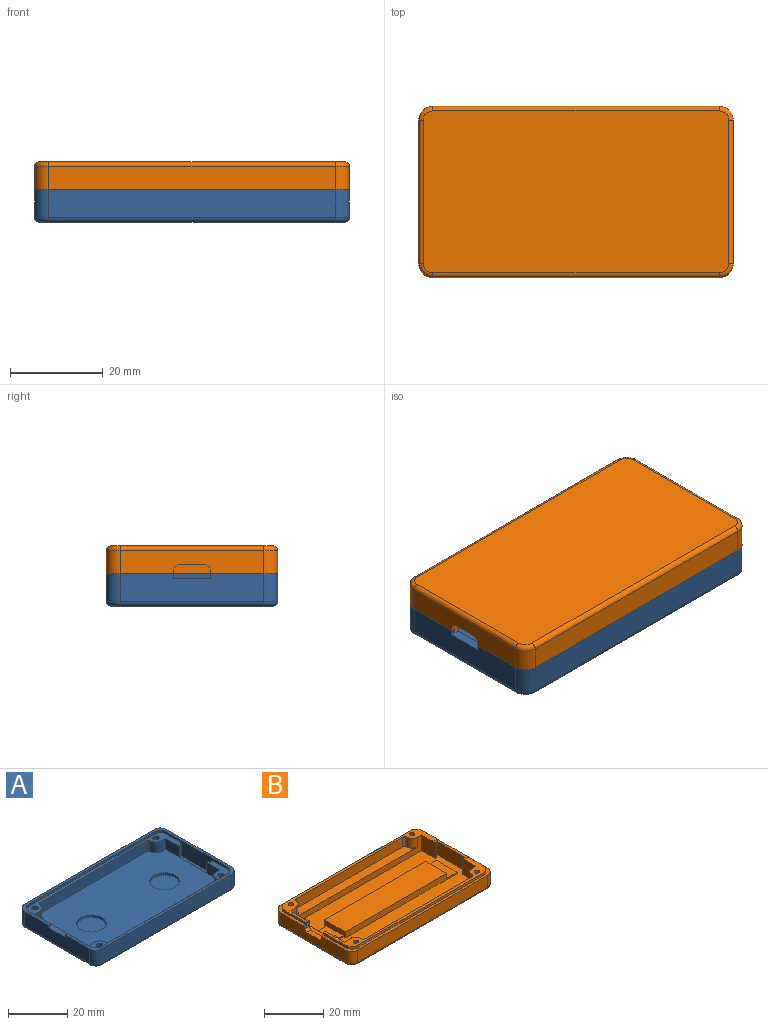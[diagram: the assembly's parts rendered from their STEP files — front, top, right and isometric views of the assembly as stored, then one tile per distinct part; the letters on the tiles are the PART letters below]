
ASSEMBLY  parts=2 mates=1
PART A: 74 faces, bbox 68.5x37.5x7 mm
  f0: plane 66x35mm, normal (0,0,-1), area 2263.6mm2, adj f43,f45,f47,f49,f52,f53,f54,f55
  f1: plane 29x6.5mm, normal (-1,0,0), area 111.5mm2, adj f12,f29,f30,f36,f51,f57,f58
  f2: plane 1x1mm, normal (0,1,0), area 1mm2, adj f6,f11,f12,f36
  f3: plane 62x6mm, normal (0,-1,0), area 372mm2, adj f12,f54,f68,f70
  f4: plane 31x6mm, normal (1,0,0), area 186mm2, adj f12,f52,f66,f68
  f5: plane 62x6mm, normal (0,1,0), area 372mm2, adj f12,f53,f64,f66
  f6: plane 31x6mm, normal (-1,0,0), area 178mm2, adj f2,f7,f12,f36,f55,f64,f70
  f7: plane 1x1mm, normal (0,-1,0), area 1mm2, adj f6,f8,f12,f36
  f8: plane 10.5x1mm, normal (1,0,0), area 10.5mm2, adj f7,f12,f36,f56
  f9: plane 60x1mm, normal (0,-1,0), area 60mm2, adj f12,f36,f56,f57
  f10: plane 60x1mm, normal (0,1,0), area 60mm2, adj f12,f36,f58,f59
  f11: plane 10.5x1mm, normal (1,0,0), area 10.5mm2, adj f2,f12,f36,f59
  f12: plane 68x37mm, normal (0,0,1), area 198mm2, adj f1,f2,f3,f4,f5,f6,f7,f8
  f13: plane 5.5x0.6mm, normal (0,1,0), area 3.3mm2, adj f14,f36,f37,f51,f72
  f14: plane 6.5x4.5mm, normal (-1,0,0), area 29.2mm2, adj f13,f15,f36,f40
  f15: plane 4.5x2mm, normal (0,1,0), area 9mm2, adj f14,f16,f36,f40
  f16: cylinder r=2.5mm len=4.5mm, axis (0,0,-1), area 17.7mm2, adj f15,f36,f40,f60
  f17: plane 51x4.5mm, normal (0,1,0), area 229.5mm2, adj f36,f40,f60,f61
  f18: cylinder r=2.5mm len=4.5mm, axis (0,0,-1), area 17.7mm2, adj f19,f36,f40,f61
  f19: plane 4.5x3mm, normal (0,1,0), area 13.5mm2, adj f18,f20,f36,f40
  f20: plane 26x4.5mm, normal (1,0,0), area 117mm2, adj f19,f21,f36,f40
  f21: plane 4.5x3mm, normal (0,-1,0), area 13.5mm2, adj f20,f22,f36,f40
  f22: cylinder r=2.5mm len=4.5mm, axis (0,0,-1), area 17.7mm2, adj f21,f36,f40,f62
  f23: plane 51x4.5mm, normal (0,-1,0), area 229.5mm2, adj f36,f40,f62,f63
  f24: cylinder r=2.5mm len=4.5mm, axis (0,0,-1), area 17.7mm2, adj f25,f36,f40,f63
  f25: plane 4.5x2mm, normal (0,-1,0), area 9mm2, adj f24,f26,f36,f40
  f26: plane 6.5x4.5mm, normal (-1,0,0), area 29.2mm2, adj f25,f27,f36,f40
  f27: plane 5.5x0.6mm, normal (0,-1,0), area 3.3mm2, adj f26,f36,f37,f51,f73
  f28: plane 5.5x0.7mm, normal (1,0,0), area 3.8mm2, adj f29,f36,f51,f73
  f29: plane 5.5x1.1mm, normal (0,-1,0), area 6mm2, adj f1,f28,f36,f51
  f30: plane 5.5x1.1mm, normal (0,1,0), area 6mm2, adj f1,f34,f36,f51
  f31: cylinder r=1.1mm len=3.5mm, axis (0,0,-1), area 24.2mm2, adj f36,f50
  f32: cylinder r=1.1mm len=3.5mm, axis (0,0,-1), area 24.2mm2, adj f36,f48
  f33: cylinder r=1.1mm len=3.5mm, axis (0,0,-1), area 24.2mm2, adj f36,f46
  f34: plane 5.5x0.7mm, normal (1,0,0), area 3.8mm2, adj f30,f36,f51,f72
  f35: cylinder r=1.1mm len=3.5mm, axis (0,0,-1), area 24.2mm2, adj f36,f44
  f36: plane 67x35mm, normal (0,0,1), area 253.3mm2, adj f1,f2,f6,f7,f8,f9,f10,f11
  f37: plane 13x1mm, normal (1,0,0), area 13mm2, adj f13,f27,f40,f51
  f38: cylinder r=5mm len=10mm, axis (0,0,-1), area 31.4mm2, adj f40,f41
  f39: cylinder r=5mm len=10mm, axis (0,0,-1), area 31.4mm2, adj f40,f42
  f40: plane 63x33mm, normal (0,0,1), area 1856.4mm2, adj f14,f15,f16,f17,f18,f19,f20,f21
  f41: plane 10x10mm, normal (0,0,1), area 78.5mm2, adj f38
  f42: plane 10x10mm, normal (0,0,1), area 78.5mm2, adj f39
  f43: cylinder r=1.85mm len=3.7mm, axis (0,0,-1), area 29.1mm2, adj f0,f44
  f44: plane 3.7x3.7mm, normal (0,0,-1), area 7mm2, adj f35,f43
  f45: cylinder r=1.85mm len=3.7mm, axis (0,0,-1), area 29.1mm2, adj f0,f46
  f46: plane 3.7x3.7mm, normal (0,0,-1), area 7mm2, adj f33,f45
  f47: cylinder r=1.85mm len=3.7mm, axis (0,0,-1), area 29.1mm2, adj f0,f48
  f48: plane 3.7x3.7mm, normal (0,0,-1), area 7mm2, adj f32,f47
  f49: cylinder r=1.85mm len=3.7mm, axis (0,0,-1), area 29.1mm2, adj f0,f50
  f50: plane 3.7x3.7mm, normal (0,0,-1), area 7mm2, adj f31,f49
  f51: plane 15x2mm, normal (0,0,1), area 28.3mm2, adj f1,f13,f27,f28,f29,f30,f34,f37
  f52: cylinder r=1mm len=31mm, axis (0,1,0), area 48.7mm2, adj f0,f4,f67,f69
  f53: cylinder r=1mm len=62mm, axis (-1,0,0), area 97.4mm2, adj f0,f5,f65,f67
  f54: cylinder r=1mm len=62mm, axis (1,0,0), area 97.4mm2, adj f0,f3,f69,f71
  f55: cylinder r=1mm len=31mm, axis (0,-1,0), area 48.7mm2, adj f0,f6,f65,f71
  f56: cylinder r=3mm len=3mm, axis (0,0,-1), area 4.7mm2, adj f8,f9,f12,f36
  f57: cylinder r=3mm len=3mm, axis (0,0,1), area 4.7mm2, adj f1,f9,f12,f36
  f58: cylinder r=3mm len=3mm, axis (0,0,-1), area 4.7mm2, adj f1,f10,f12,f36
  f59: cylinder r=3mm len=3mm, axis (0,0,1), area 4.7mm2, adj f10,f11,f12,f36
  f60: cylinder r=1mm len=4.5mm, axis (0,0,-1), area 7.1mm2, adj f16,f17,f36,f40
  f61: cylinder r=1mm len=4.5mm, axis (0,0,1), area 7.1mm2, adj f17,f18,f36,f40
  f62: cylinder r=1mm len=4.5mm, axis (0,0,1), area 7.1mm2, adj f22,f23,f36,f40
  f63: cylinder r=1mm len=4.5mm, axis (0,0,-1), area 7.1mm2, adj f23,f24,f36,f40
  f64: cylinder r=3mm len=6mm, axis (0,0,1), area 28.3mm2, adj f5,f6,f12,f65
  f65: torus R=2mm, axis (0,0,1), area 6.5mm2, adj f0,f53,f55,f64
  f66: cylinder r=3mm len=6mm, axis (0,0,-1), area 28.3mm2, adj f4,f5,f12,f67
  f67: torus R=2mm, axis (0,0,1), area 6.5mm2, adj f0,f52,f53,f66
  f68: cylinder r=3mm len=6mm, axis (0,0,1), area 28.3mm2, adj f3,f4,f12,f69
  f69: torus R=2mm, axis (0,0,1), area 6.5mm2, adj f0,f52,f54,f68
  f70: cylinder r=3mm len=6mm, axis (0,0,-1), area 28.3mm2, adj f3,f6,f12,f71
  f71: torus R=2mm, axis (0,0,1), area 6.5mm2, adj f0,f54,f55,f70
  f72: plane 5.5x0.3mm, normal (0.71,0.71,0), area 2.3mm2, adj f13,f34,f36,f51
  f73: plane 5.5x0.3mm, normal (0.71,-0.71,0), area 2.3mm2, adj f27,f28,f36,f51
PART B: 86 faces, bbox 68.5x37.5x7 mm
  f0: plane 62.5x26mm, normal (0,0,1), area 1018.3mm2, adj f2,f10,f18,f19,f20,f22,f25,f29
  f1: plane 66x35mm, normal (0,0,-1), area 2306.6mm2, adj f52,f53,f54,f55,f69,f71,f73,f75
  f2: plane 15x5.5mm, normal (-1,0,0), area 82.5mm2, adj f0,f9,f18,f25
  f3: plane 2x2mm, normal (0,1,0), area 3mm2, adj f7,f9,f14,f15,f24,f64
  f4: plane 62x5mm, normal (0,-1,0), area 310mm2, adj f9,f54,f72,f74
  f5: plane 31x5mm, normal (1,0,0), area 155mm2, adj f9,f52,f70,f72
  f6: plane 62x5mm, normal (0,1,0), area 310mm2, adj f9,f53,f68,f70
  f7: plane 31x5mm, normal (-1,0,0), area 140mm2, adj f3,f8,f9,f41,f55,f64,f65,f68
  f8: plane 2x2mm, normal (0,-1,0), area 3mm2, adj f7,f9,f14,f28,f38,f65
  f9: plane 68x37mm, normal (0,0,1), area 198mm2, adj f2,f3,f4,f5,f6,f7,f8,f15
  f10: plane 62.99x6.5mm, normal (0,1,0), area 171.2mm2, adj f0,f11,f13,f14,f22,f24,f40,f46
  f11: cylinder r=2.5mm len=4mm, axis (0,0,-1), area 15.7mm2, adj f10,f24,f40,f60
  f12: plane 51x4mm, normal (0,1,0), area 204mm2, adj f24,f40,f60,f61
  f13: cylinder r=2.5mm len=4mm, axis (0,0,-1), area 15.7mm2, adj f10,f24,f40,f61
  f14: plane 26x4mm, normal (1,0,0), area 81mm2, adj f3,f8,f10,f24,f29,f38,f41,f51
  f15: plane 10.5x1mm, normal (-1,0,0), area 10.5mm2, adj f3,f9,f24,f56
  f16: plane 60x1mm, normal (0,-1,0), area 60mm2, adj f9,f24,f56,f57
  f17: plane 7x1mm, normal (1,0,0), area 7mm2, adj f9,f18,f24,f57
  f18: plane 6.5x1.1mm, normal (0,1,0), area 7.2mm2, adj f0,f2,f17,f19,f24
  f19: plane 6.5x0.7mm, normal (1,0,0), area 4.5mm2, adj f0,f18,f24,f66
  f20: plane 6.5x0.6mm, normal (0,1,0), area 3.9mm2, adj f0,f22,f24,f66
  f21: cylinder r=0.9mm len=6mm, axis (0,0,-1), area 33.9mm2, adj f24,f42
  f22: plane 6.5x6.5mm, normal (-1,0,0), area 42.3mm2, adj f0,f10,f20,f24
  f23: cylinder r=0.9mm len=6mm, axis (0,0,-1), area 33.9mm2, adj f24,f43
  f24: plane 66x13.5mm, normal (0,0,1), area 121.2mm2, adj f3,f10,f11,f12,f13,f14,f15,f16
  f25: plane 6.5x1.1mm, normal (0,-1,0), area 7.2mm2, adj f0,f2,f26,f37,f38
  f26: plane 7x1mm, normal (1,0,0), area 7mm2, adj f9,f25,f38,f59
  f27: plane 60x1mm, normal (0,1,0), area 60mm2, adj f9,f38,f58,f59
  f28: plane 10.5x1mm, normal (-1,0,0), area 10.5mm2, adj f8,f9,f38,f58
  f29: plane 63x6.5mm, normal (0,-1,0), area 171.3mm2, adj f0,f14,f30,f32,f33,f38,f39,f46
  f30: cylinder r=2.5mm len=4mm, axis (0,0,-1), area 15.7mm2, adj f29,f38,f39,f63
  f31: plane 50.99x4mm, normal (0,-1,0), area 204mm2, adj f38,f39,f62,f63
  f32: cylinder r=2.5mm len=4mm, axis (0,0,-1), area 15.7mm2, adj f29,f38,f39,f62
  f33: plane 6.5x6.5mm, normal (-1,0,0), area 42.3mm2, adj f0,f29,f34,f38
  f34: plane 6.5x0.6mm, normal (0,-1,0), area 3.9mm2, adj f0,f33,f38,f67
  f35: cylinder r=0.9mm len=6mm, axis (0,0,-1), area 33.9mm2, adj f38,f45
  f36: cylinder r=0.9mm len=6mm, axis (0,0,-1), area 33.9mm2, adj f38,f44
  f37: plane 6.5x0.7mm, normal (1,0,0), area 4.6mm2, adj f0,f25,f38,f67
  f38: plane 66x13.5mm, normal (0,0,1), area 121.2mm2, adj f8,f14,f25,f26,f27,f28,f29,f30
  f39: plane 57.99x3.5mm, normal (0,0,1), area 187.7mm2, adj f29,f30,f31,f32,f62,f63
  f40: plane 58x3.5mm, normal (0,0,1), area 187.8mm2, adj f10,f11,f12,f13,f60,f61
  f41: plane 6x2mm, normal (0,0,1), area 12mm2, adj f7,f14,f64,f65
  f42: plane 1.8x1.8mm, normal (0,0,1), area 2.5mm2, adj f21
  f43: plane 1.8x1.8mm, normal (0,0,1), area 2.5mm2, adj f23
  f44: plane 1.8x1.8mm, normal (0,0,1), area 2.5mm2, adj f36
  f45: plane 1.8x1.8mm, normal (0,0,1), area 2.5mm2, adj f35
  f46: plane 26x4.5mm, normal (1,0,0), area 67.9mm2, adj f0,f10,f29,f47,f48,f49,f50,f51
  f47: cylinder r=1mm len=2mm, axis (0,0,-1), area 8.4mm2, adj f46,f48,f51
  f48: plane 2x1.5mm, normal (0,0,1), area 2.5mm2, adj f46,f47
  f49: cylinder r=1mm len=2mm, axis (0,0,-1), area 8.4mm2, adj f46,f50,f51
  f50: plane 2x1.5mm, normal (0,0,1), area 2.5mm2, adj f46,f49
  f51: plane 26x2.5mm, normal (0,0,1), area 59.9mm2, adj f10,f14,f29,f46,f47,f49
  f52: cylinder r=1mm len=31mm, axis (0,1,0), area 48.7mm2, adj f1,f5,f71,f73
  f53: cylinder r=1mm len=62mm, axis (-1,0,0), area 97.4mm2, adj f1,f6,f69,f71
  f54: cylinder r=1mm len=62mm, axis (1,0,0), area 97.4mm2, adj f1,f4,f73,f75
  f55: cylinder r=1mm len=31mm, axis (0,-1,0), area 48.7mm2, adj f1,f7,f69,f75
  f56: cylinder r=3mm len=3mm, axis (0,0,-1), area 4.7mm2, adj f9,f15,f16,f24
  f57: cylinder r=3mm len=3mm, axis (0,0,1), area 4.7mm2, adj f9,f16,f17,f24
  f58: cylinder r=3mm len=3mm, axis (0,0,1), area 4.7mm2, adj f9,f27,f28,f38
  f59: cylinder r=3mm len=3mm, axis (0,0,1), area 4.7mm2, adj f9,f26,f27,f38
  f60: cylinder r=1mm len=4mm, axis (0,0,-1), area 6.3mm2, adj f11,f12,f24,f40
  f61: cylinder r=1mm len=4mm, axis (0,0,1), area 6.3mm2, adj f12,f13,f24,f40
  f62: cylinder r=1mm len=4mm, axis (0,0,-1), area 6.3mm2, adj f31,f32,f38,f39
  f63: cylinder r=1mm len=4mm, axis (0,0,1), area 6.3mm2, adj f30,f31,f38,f39
  f64: plane 2x1mm, normal (0,0.71,0.71), area 2.8mm2, adj f3,f7,f14,f41
  f65: plane 2x1mm, normal (0,-0.71,0.71), area 2.8mm2, adj f7,f8,f14,f41
  f66: plane 6.5x0.3mm, normal (0.71,0.71,0), area 2.8mm2, adj f0,f19,f20,f24
  f67: plane 6.5x0.3mm, normal (0.71,-0.71,0), area 2.8mm2, adj f0,f34,f37,f38
  f68: cylinder r=3mm len=5mm, axis (0,0,1), area 23.6mm2, adj f6,f7,f9,f69
  f69: torus R=2mm, axis (0,0,1), area 6.5mm2, adj f1,f53,f55,f68
  f70: cylinder r=3mm len=5mm, axis (0,0,-1), area 23.6mm2, adj f5,f6,f9,f71
  f71: torus R=2mm, axis (0,0,1), area 6.5mm2, adj f1,f52,f53,f70
  f72: cylinder r=3mm len=5mm, axis (0,0,1), area 23.6mm2, adj f4,f5,f9,f73
  f73: torus R=2mm, axis (0,0,1), area 6.5mm2, adj f1,f52,f54,f72
  f74: cylinder r=3mm len=5mm, axis (0,0,-1), area 23.6mm2, adj f4,f7,f9,f75
  f75: torus R=2mm, axis (0,0,1), area 6.5mm2, adj f1,f54,f55,f74
  f76: plane 6x0.5mm, normal (0,1,0), area 3mm2, adj f0,f46,f78,f84
  f77: plane 6x0.5mm, normal (0,-1,0), area 3mm2, adj f0,f46,f78,f84
  f78: plane 8x6mm, normal (0,0,1), area 48mm2, adj f46,f76,f77,f84
  f79: plane 10x0.5mm, normal (1,0,0), area 5mm2, adj f0,f80,f81,f82
  f80: plane 53.5x2.5mm, normal (0,1,0), area 123.7mm2, adj f0,f79,f82,f83,f84,f85
  f81: plane 53.5x2.5mm, normal (0,-1,0), area 123.7mm2, adj f0,f79,f82,f83,f84,f85
  f82: plane 10x5mm, normal (0,0,1), area 50mm2, adj f79,f80,f81,f85
  f83: plane 48.5x10mm, normal (0,0,1), area 485mm2, adj f80,f81,f84,f85
  f84: plane 10x2.5mm, normal (-1,0,0), area 21mm2, adj f0,f76,f77,f78,f80,f81,f83
  f85: plane 10x2mm, normal (1,0,0), area 20mm2, adj f80,f81,f82,f83
PLACE A t=(-15.53,17.9,-8.19)mm
PLACE B rot(axis=(1,0,0),180deg) t=(-35.62,-2.55,4.81)mm
MATE fastened B.f13 <-> A.f22  axis (0,0,-1) through (-34.62,25.61,-2.19)mm
